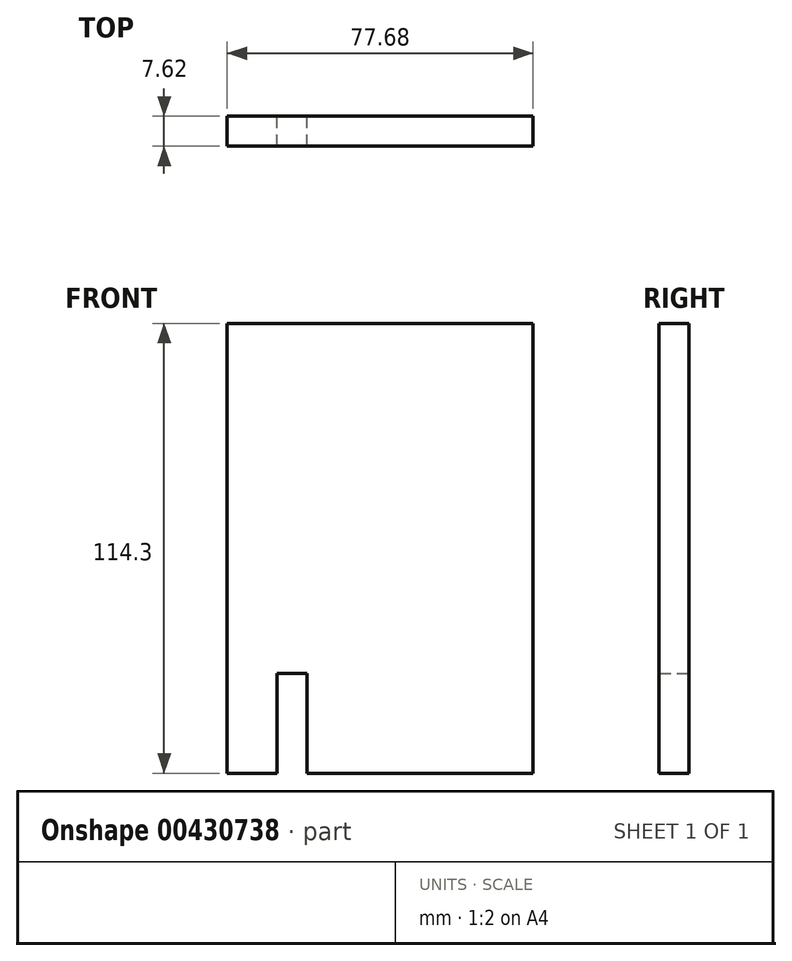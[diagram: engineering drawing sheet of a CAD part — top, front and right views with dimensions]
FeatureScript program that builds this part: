
annotation { "Feature Type Name" : "Feature", "Feature Type Description" : "" }
export const myFeature = defineFeature(function(context is Context, id is Id, definition is map)
    precondition{}
    {
        {
            var Q0;
            Q0=qCreatedBy(makeId("Front.planeOp"),FACE);
            var sketch = newSketch(context, id + "F0", { "sketchPlane" : qUnion([Q0])});
            skLineSegment(sketch, "E0.bottom", {"start": v(-139.7, 114.3) * mm, "end": v(0, 114.3) * mm});
            skLineSegment(sketch, "E0.top", {"start": v(-139.7, 0) * mm, "end": v(0, 0) * mm});
            skLineSegment(sketch, "E0.left", {"start": v(-139.7, 114.3) * mm, "end": v(-139.7, 0) * mm});
            skLineSegment(sketch, "E0.right", {"start": v(0, 114.3) * mm, "end": v(0, 0) * mm});
            skLineSegment(sketch, "E1.bottom", {"start": v(101.4, 59.15) * mm, "end": v(95.04, 59.15) * mm});
            skLineSegment(sketch, "E1.top", {"start": v(101.4, 33.75) * mm, "end": v(95.04, 33.75) * mm});
            skLineSegment(sketch, "E1.left", {"start": v(95.04, 59.15) * mm, "end": v(95.04, 33.75) * mm});
            skLineSegment(sketch, "E1.right", {"start": v(101.4, 59.15) * mm, "end": v(101.4, 33.75) * mm});
            skLineSegment(sketch, "E2.bottom", {"start": v(-197.06, 25.4) * mm, "end": v(-204.68, 25.4) * mm});
            skLineSegment(sketch, "E2.top", {"start": v(-197.06, 0) * mm, "end": v(-204.68, 0) * mm});
            skLineSegment(sketch, "E2.left", {"start": v(-197.06, 25.4) * mm, "end": v(-197.06, 0) * mm});
            skLineSegment(sketch, "E2.right", {"start": v(-204.68, 25.4) * mm, "end": v(-204.68, 0) * mm});
            skLineSegment(sketch, "E3.bottom", {"start": v(-139.7, 0) * mm, "end": v(-217.38, 0) * mm});
            skLineSegment(sketch, "E3.top", {"start": v(-139.7, 114.3) * mm, "end": v(-217.38, 114.3) * mm});
            skLineSegment(sketch, "E3.left", {"start": v(-139.7, 0) * mm, "end": v(-139.7, 114.3) * mm});
            skLineSegment(sketch, "E3.right", {"start": v(-217.38, 0) * mm, "end": v(-217.38, 114.3) * mm});
            skSolve(sketch);
        }
        {
            var Q0;
            Q0=makeQuery(id+"F0.imprint","IMPRINT",FACE,{"disambiguationData":[TD([[makeQuery(id+"F0.imprint","IMPRINT",EDGE,{"derivedFrom":sQuery(id+"F0.wireOp",EDGE,"E2.bottom")}),-1.0]])]});
            extrude(context, id + "F1", {"entities" : qUnion([Q0]), "depth" : 7.62 * mm, "offsetDistance" : 25.4 * mm});
        }
    });
